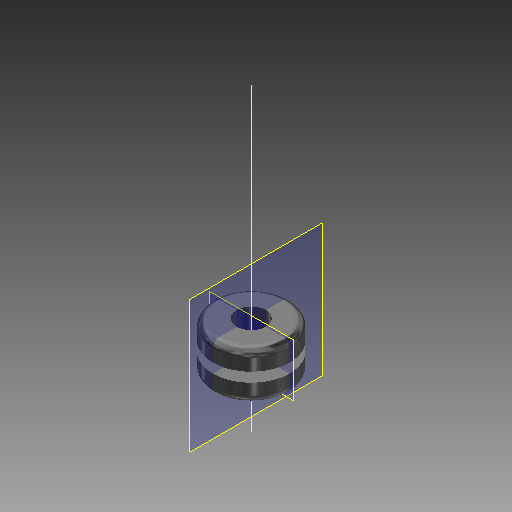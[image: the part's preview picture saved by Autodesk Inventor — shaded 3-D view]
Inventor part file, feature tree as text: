
AUTODESK INVENTOR PART (.ipt)
format: ipt  version: 2017 (Build 210142000, 142)  size: 143,360 bytes
history: native  units: in
note: dims shown in document units (in); Inventor stores cm internally (conversion verified against a paired STEP export)
features: plane x2, revolve x1, sketch x1, other x1
ambient origin geometry x8: Origin, YZ Plane, XZ Plane, XY Plane, X Axis, Y Axis, Z Axis, Center Point
bodies: Solid1 (feature_tree)
feature tree (5):
  plane  "Work Plane2"
  revolve  "Revolution1"  Angle=90.0deg
  plane  "Work Plane3"
  sketch  "Sketch2"  dims[d0=0.05in d1=90.0deg d2=0.05in d4=0.1562in d5=0.3125in d6=90.0deg]
  other  "Work Axis2"
